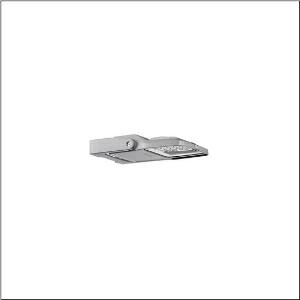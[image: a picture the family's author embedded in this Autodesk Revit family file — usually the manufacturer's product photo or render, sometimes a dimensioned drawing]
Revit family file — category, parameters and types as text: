
# Revit family: floodlight_fl_21_iq_micro___pl43_5xa7762a4a2a_306a
name_source: partatom
category: Lighting Fixtures
units: mm (PartAtom-declared; Revit-internal decimal feet)

## family parameters
Cut with Voids When Loaded = No
Host = Face
Light Source = No
Part Type = Normal
Room Calculation Point = No
Round Connector Dimension = Use Diameter
Shared = No

## types (1)
- --- (1 x LED, 3170 lm, 23.1 W, 4000K)
    Apparent Load = 23 VA
    CIE Flux Codes = 29 80 99 100 100
    Color Rendering = 70
    Color Temperature = 4000K
    Default Elevation = 1800 mm
    Description = Floodlight FL 21 iQ micro, floodlight, primary light control with lens, of PMMA, primary optical cover: protective disc, of toughened safety glass, transparent, light distribution: PL43, light emission: direct distribution, installation type: surface-mounted, LED, High Power LED, rated luminous flux: 3.170lm, luminous efficacy: 137lm/W, light colour: 740, colour temperature: 4000K, control: Auto-Match, Temp-Guard, Night-Set, Smart-Wire, Desk-Remote (wireless, voltage-free reading and setting of iQ features in the workshop via application-optimized NFC function/RFID function), optimised constant luminous flux control (CLO 2.0), Street-Remote, with terminal, 6-pole, mains connection: 220..240V, AC, 50/60Hz, start of lifetime: 23W, end of service life: 24W, reduction: 11W, luminaire housing, of diecast aluminium, powder-coated, Siteco® metallic grey (DB 702S), corrosivity category C5 mid according to DIN EN ISO 12944, sealing non-destructively replaceable, design bracket, of diecast aluminium, powder-coated, Siteco® metallic grey (DB 702S), protection rating (complete): IP66, insulation class (complete): insulation class II (safety insulation), certification: CE, ENEC, VDE, protection symbol: D, impact resistance: IK07, permissible operating ambient temperature: -40..+40°C, permissible operating ambient temperature for outdoor applications: -40..+50°C, standard: DIN EN 12944, LABS conformity tested according to VDMA 24364:2018-05, packaging unit: 1 piece

Light Distribution: PL43
    Height = 65 mm
    Lamp = 1 x LED
    Lamp Light Flux = 3170 lm
    Lamp Power = 23.1 W
    Lamp count = 1
    Length = 312 mm
    Luminous efficacy = 137 lm/W
    Manufacturer = Siteco
    ModVariant = No
    Model = 5XA7762A4A2A
    Mounting Place = Wall
    Mounting Type = Surface mounted
    Number of Poles = 1
    OnlyDefault = Yes
    Power Factor = 1
    Product Name = Floodlight FL 21 iQ micro | PL43
    Product group = floodlight | wall mounted
    ProductGroupID = 2001
    Protection Class = Protection class II
    Protection Degree = IP 66
    RLX_Detail_Level = 1
    RLX_Emergency_Light_Flux = 0 lm
    RLX_Emergency_Type = 0
    RLX_Emergency_Type_DB = No
    RlxData = <blob elided: 97425 chars, md5=2679889f>
    Socket = socket
    Standby Power = 0 W
    System Light Flux = 3170 lm
    System Power = 23 W
    Type Comments = factory setting: luminous flux: 100 % | dim-lin: 254 | 455 mA
    Type Image = l_1006878.jpg
    URL = http://relux.com
    VarID = @adj_147767
    Voltage = 0 V
    Weight = 0.00 kg
    Width = 230 mm

## geometry (parser evidence)
native form markers: Blend x4, Sweep x13
no freeform markers — native parametric forms only
